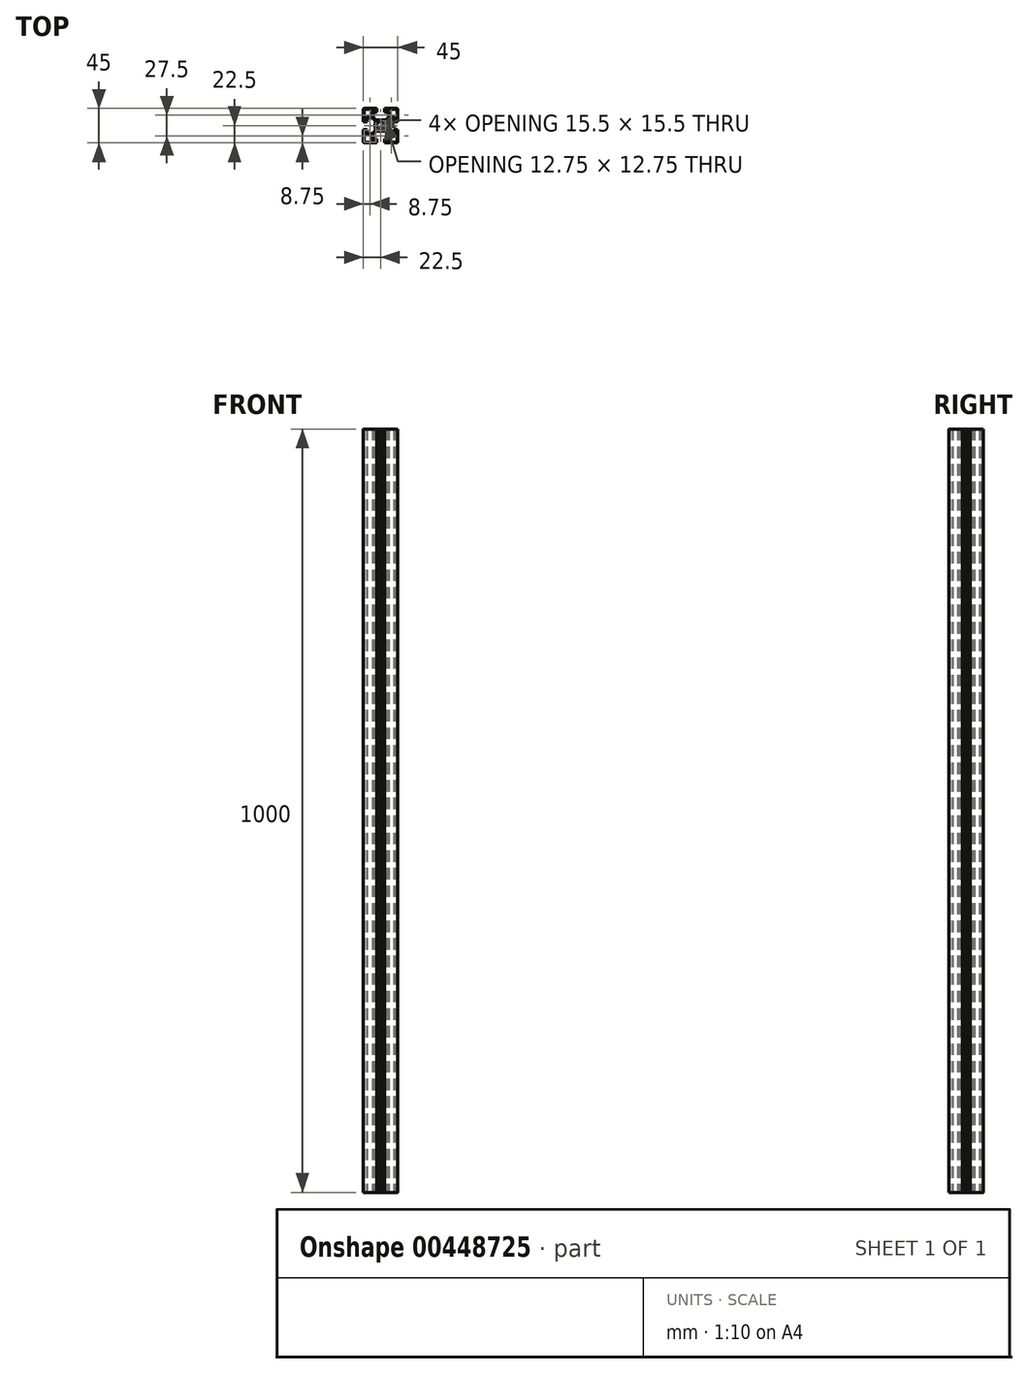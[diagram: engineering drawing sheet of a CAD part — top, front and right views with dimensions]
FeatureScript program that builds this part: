
annotation { "Feature Type Name" : "Feature", "Feature Type Description" : "" }
export const myFeature = defineFeature(function(context is Context, id is Id, definition is map)
    precondition{}
    {
        {
            var Q0;
            Q0=qCreatedBy(makeId("Top.planeOp"),FACE);
            var sketch = newSketch(context, id + "F0", { "sketchPlane" : qUnion([Q0])});
            skPoint(sketch, "E0.middle", {"position": v(0, 0) * mm});
            skLineSegment(sketch, "E1", {"start": v(0, -50.6) * mm, "end": v(0, -50.6) * mm});
            skPoint(sketch, "E1.endSnap0", {"position": v(0, -22.4) * mm});
            skLineSegment(sketch, "E2", {"start": v(-31.12, 0) * mm, "end": v(33.93, 0) * mm, "construction": true});
            skLineSegment(sketch, "E3.0", {"start": v(-5, 22.5) * mm, "end": v(-5, 17.5) * mm});
            skLineSegment(sketch, "E4.0", {"start": v(-22.5, 5) * mm, "end": v(-17.5, 5) * mm});
            skLineSegment(sketch, "E5.trimOffspring", {"start": v(-5, 22.5) * mm, "end": v(-21.5, 22.5) * mm});
            skLineSegment(sketch, "E6.trimOffspring", {"start": v(-22.5, 5) * mm, "end": v(-22.5, 21.5) * mm});
            skLineSegment(sketch, "E7.0", {"start": v(-10.7, 10) * mm, "end": v(-7.25, 6.54) * mm});
            skLineSegment(sketch, "E8.0", {"start": v(-21.5, 6.5) * mm, "end": v(-21.5, 21) * mm});
            skLineSegment(sketch, "E9.0", {"start": v(-6.5, 21.5) * mm, "end": v(-21, 21.5) * mm});
            skLineSegment(sketch, "E10.0", {"start": v(-6, 21) * mm, "end": v(-6, 19.04) * mm});
            skLineSegment(sketch, "E11.0", {"start": v(-22.5, 0) * mm, "end": v(22.5, 0) * mm});
            skLineSegment(sketch, "E12.0", {"start": v(-21, 6) * mm, "end": v(-19, 6) * mm});
            skLineSegment(sketch, "E13.trimOffspring", {"start": v(-9.63, 10.7) * mm, "end": v(-6.54, 7.25) * mm});
            skLineSegment(sketch, "E14.trimOffspring", {"start": v(-6.5, 18.54) * mm, "end": v(-10.5, 18.56) * mm});
            skLineSegment(sketch, "E15.trimOffspring", {"start": v(-5, 17.5) * mm, "end": v(-9.63, 17.5) * mm});
            skLineSegment(sketch, "E16.trimOffspring", {"start": v(-18.5, 6.5) * mm, "end": v(-18.5, 10.5) * mm});
            skLineSegment(sketch, "E17.trimOffspring", {"start": v(-17.5, 5) * mm, "end": v(-17.5, 10) * mm});
            skLineSegment(sketch, "E18.trimOffspring", {"start": v(-11, 11.5) * mm, "end": v(-11, 18.06) * mm});
            skLineSegment(sketch, "E19.trimOffspring", {"start": v(-11.5, 11) * mm, "end": v(-18, 11) * mm});
            skLineSegment(sketch, "E20.trimOffspring", {"start": v(-9.63, 10.7) * mm, "end": v(-9.63, 17.5) * mm});
            skLineSegment(sketch, "E21.trimOffspring", {"start": v(-10.7, 10) * mm, "end": v(-17.5, 10) * mm});
            skPoint(sketch, "E22.visualSharp", {"position": v(-22.5, 22.5) * mm});
            skArc(sketch, "E22.filletArc", {"start": v(-21.5, 22.5) * mm, "mid": v(-22.2, 22.2) * mm, "end": v(-22.5, 21.5) * mm});
            skArc(sketch, "E23.filletArc", {"start": v(-21, 21.5) * mm, "mid": v(-21.35, 21.35) * mm, "end": v(-21.5, 21) * mm});
            skPoint(sketch, "E24.visualSharp", {"position": v(-21.5, 6) * mm});
            skArc(sketch, "E24.filletArc", {"start": v(-21.5, 6.5) * mm, "mid": v(-21.35, 6.15) * mm, "end": v(-21, 6) * mm});
            skPoint(sketch, "E25.visualSharp", {"position": v(-18.5, 6) * mm});
            skArc(sketch, "E25.filletArc", {"start": v(-19, 6) * mm, "mid": v(-18.65, 6.15) * mm, "end": v(-18.5, 6.5) * mm});
            skPoint(sketch, "E26.visualSharp", {"position": v(-18.5, 11) * mm});
            skArc(sketch, "E26.filletArc", {"start": v(-18, 11) * mm, "mid": v(-18.35, 10.85) * mm, "end": v(-18.5, 10.5) * mm});
            skPoint(sketch, "E27.visualSharp", {"position": v(-11, 11) * mm});
            skArc(sketch, "E27.filletArc", {"start": v(-11.5, 11) * mm, "mid": v(-11.15, 11.15) * mm, "end": v(-11, 11.5) * mm});
            skPoint(sketch, "E28.visualSharp", {"position": v(-11, 18.56) * mm});
            skArc(sketch, "E28.filletArc", {"start": v(-10.5, 18.56) * mm, "mid": v(-10.85, 18.41) * mm, "end": v(-11, 18.06) * mm});
            skPoint(sketch, "E29.visualSharp", {"position": v(-6, 18.53) * mm});
            skArc(sketch, "E29.filletArc", {"start": v(-6.5, 18.54) * mm, "mid": v(-6.15, 18.68) * mm, "end": v(-6, 19.04) * mm});
            skPoint(sketch, "E30.visualSharp", {"position": v(-6, 21.5) * mm});
            skArc(sketch, "E30.filletArc", {"start": v(-6, 21) * mm, "mid": v(-6.15, 21.35) * mm, "end": v(-6.5, 21.5) * mm});
            skPoint(sketch, "E31.1.0", {"position": v(-18.5, -11) * mm});
            skLineSegment(sketch, "E31.1.1", {"start": v(-5, -17.5) * mm, "end": v(-10, -17.5) * mm});
            skLineSegment(sketch, "E31.1.2", {"start": v(-21.5, -6.5) * mm, "end": v(-21.5, -21) * mm});
            skLineSegment(sketch, "E31.1.3", {"start": v(-6.5, -21.5) * mm, "end": v(-21, -21.5) * mm});
            skLineSegment(sketch, "E31.1.4", {"start": v(-10, -10.7) * mm, "end": v(-6.54, -7.25) * mm});
            skLineSegment(sketch, "E31.1.5", {"start": v(-5, -22.5) * mm, "end": v(-21.5, -22.5) * mm});
            skLineSegment(sketch, "E31.1.6", {"start": v(-22.5, -5) * mm, "end": v(-22.5, -21.5) * mm});
            skPoint(sketch, "E31.1.7", {"position": v(-11, -11) * mm});
            skLineSegment(sketch, "E31.1.8", {"start": v(-6.5, -18.5) * mm, "end": v(-10.5, -18.5) * mm});
            skLineSegment(sketch, "E31.1.9", {"start": v(-17.5, -5) * mm, "end": v(-17.5, -10) * mm});
            skLineSegment(sketch, "E31.1.10", {"start": v(-18.5, -6.5) * mm, "end": v(-18.5, -10.5) * mm});
            skPoint(sketch, "E31.1.11", {"position": v(-18.5, -6) * mm});
            skPoint(sketch, "E31.1.12", {"position": v(-21.5, -21.5) * mm});
            skPoint(sketch, "E31.1.13", {"position": v(-11, -18.5) * mm});
            skLineSegment(sketch, "E31.1.14", {"start": v(-10, -10.7) * mm, "end": v(-10, -17.5) * mm});
            skLineSegment(sketch, "E31.1.15", {"start": v(-10.7, -10) * mm, "end": v(-7.25, -6.54) * mm});
            skLineSegment(sketch, "E31.1.16", {"start": v(-5, -22.5) * mm, "end": v(-5, -17.5) * mm});
            skLineSegment(sketch, "E31.1.17", {"start": v(-10.7, -10) * mm, "end": v(-17.5, -10) * mm});
            skPoint(sketch, "E31.1.18", {"position": v(-21.5, -6) * mm});
            skPoint(sketch, "E31.1.19", {"position": v(-6, -18.5) * mm});
            skLineSegment(sketch, "E31.1.20", {"start": v(-11, -11.5) * mm, "end": v(-11, -18) * mm});
            skLineSegment(sketch, "E31.1.21", {"start": v(-11.5, -11) * mm, "end": v(-18, -11) * mm});
            skPoint(sketch, "E31.1.22", {"position": v(-6, -21.5) * mm});
            skPoint(sketch, "E31.1.23", {"position": v(0.07, -0.4) * mm});
            skLineSegment(sketch, "E31.1.24", {"start": v(-22.5, -5) * mm, "end": v(-17.5, -5) * mm});
            skPoint(sketch, "E31.1.25", {"position": v(-22.5, -22.5) * mm});
            skArc(sketch, "E31.1.26", {"start": v(-22.5, -21.5) * mm, "mid": v(-22.2, -22.2) * mm, "end": v(-21.5, -22.5) * mm});
            skPoint(sketch, "E31.1.27", {"position": v(0.07, -0.4) * mm});
            skLineSegment(sketch, "E31.1.28", {"start": v(-6, -21) * mm, "end": v(-6, -19) * mm});
            skLineSegment(sketch, "E31.1.29", {"start": v(-21, -6) * mm, "end": v(-19, -6) * mm});
            skPoint(sketch, "E31.1.30", {"position": v(0.07, -0.4) * mm});
            skArc(sketch, "E31.1.31", {"start": v(-21.5, -21) * mm, "mid": v(-21.35, -21.35) * mm, "end": v(-21, -21.5) * mm});
            skPoint(sketch, "E31.1.32", {"position": v(0.07, -0.4) * mm});
            skArc(sketch, "E31.1.33", {"start": v(-6.5, -21.5) * mm, "mid": v(-6.15, -21.35) * mm, "end": v(-6, -21) * mm});
            skArc(sketch, "E31.1.34", {"start": v(-18.5, -6.5) * mm, "mid": v(-18.65, -6.15) * mm, "end": v(-19, -6) * mm});
            skArc(sketch, "E31.1.35", {"start": v(-11, -18) * mm, "mid": v(-10.85, -18.35) * mm, "end": v(-10.5, -18.5) * mm});
            skArc(sketch, "E31.1.36", {"start": v(-21, -6) * mm, "mid": v(-21.35, -6.15) * mm, "end": v(-21.5, -6.5) * mm});
            skArc(sketch, "E31.1.37", {"start": v(-11, -11.5) * mm, "mid": v(-11.15, -11.15) * mm, "end": v(-11.5, -11) * mm});
            skArc(sketch, "E31.1.38", {"start": v(-6, -19) * mm, "mid": v(-6.15, -18.65) * mm, "end": v(-6.5, -18.5) * mm});
            skArc(sketch, "E31.1.39", {"start": v(-18.5, -10.5) * mm, "mid": v(-18.35, -10.85) * mm, "end": v(-18, -11) * mm});
            skPoint(sketch, "E31.2.0", {"position": v(11, -18.5) * mm});
            skLineSegment(sketch, "E31.2.1", {"start": v(17.5, -5) * mm, "end": v(17.5, -10) * mm});
            skLineSegment(sketch, "E31.2.2", {"start": v(6.5, -21.5) * mm, "end": v(21, -21.5) * mm});
            skLineSegment(sketch, "E31.2.3", {"start": v(21.5, -6.5) * mm, "end": v(21.5, -21) * mm});
            skLineSegment(sketch, "E31.2.4", {"start": v(10.7, -10) * mm, "end": v(7.25, -6.54) * mm});
            skLineSegment(sketch, "E31.2.5", {"start": v(22.5, -5) * mm, "end": v(22.5, -21.5) * mm});
            skLineSegment(sketch, "E31.2.6", {"start": v(5, -22.5) * mm, "end": v(21.5, -22.5) * mm});
            skPoint(sketch, "E31.2.7", {"position": v(11, -11) * mm});
            skLineSegment(sketch, "E31.2.8", {"start": v(18.5, -6.5) * mm, "end": v(18.5, -10.5) * mm});
            skLineSegment(sketch, "E31.2.9", {"start": v(5, -17.5) * mm, "end": v(10, -17.5) * mm});
            skLineSegment(sketch, "E31.2.10", {"start": v(6.5, -18.5) * mm, "end": v(10.5, -18.5) * mm});
            skPoint(sketch, "E31.2.11", {"position": v(6, -18.5) * mm});
            skPoint(sketch, "E31.2.12", {"position": v(21.5, -21.5) * mm});
            skPoint(sketch, "E31.2.13", {"position": v(18.5, -11) * mm});
            skLineSegment(sketch, "E31.2.14", {"start": v(10.7, -10) * mm, "end": v(17.5, -10) * mm});
            skLineSegment(sketch, "E31.2.15", {"start": v(10, -10.7) * mm, "end": v(6.54, -7.25) * mm});
            skLineSegment(sketch, "E31.2.16", {"start": v(22.5, -5) * mm, "end": v(17.5, -5) * mm});
            skLineSegment(sketch, "E31.2.17", {"start": v(10, -10.7) * mm, "end": v(10, -17.5) * mm});
            skPoint(sketch, "E31.2.18", {"position": v(6, -21.5) * mm});
            skPoint(sketch, "E31.2.19", {"position": v(18.5, -6) * mm});
            skLineSegment(sketch, "E31.2.20", {"start": v(11.5, -11) * mm, "end": v(18, -11) * mm});
            skLineSegment(sketch, "E31.2.21", {"start": v(11, -11.5) * mm, "end": v(11, -18) * mm});
            skPoint(sketch, "E31.2.22", {"position": v(21.5, -6) * mm});
            skLineSegment(sketch, "E31.2.24", {"start": v(5, -22.5) * mm, "end": v(5, -17.5) * mm});
            skPoint(sketch, "E31.2.25", {"position": v(22.5, -22.5) * mm});
            skArc(sketch, "E31.2.26", {"start": v(21.5, -22.5) * mm, "mid": v(22.2, -22.2) * mm, "end": v(22.5, -21.5) * mm});
            skLineSegment(sketch, "E31.2.28", {"start": v(21, -6) * mm, "end": v(19, -6) * mm});
            skLineSegment(sketch, "E31.2.29", {"start": v(6, -21) * mm, "end": v(6, -19) * mm});
            skArc(sketch, "E31.2.31", {"start": v(21, -21.5) * mm, "mid": v(21.35, -21.35) * mm, "end": v(21.5, -21) * mm});
            skArc(sketch, "E31.2.33", {"start": v(21.5, -6.5) * mm, "mid": v(21.35, -6.15) * mm, "end": v(21, -6) * mm});
            skArc(sketch, "E31.2.34", {"start": v(6.5, -18.5) * mm, "mid": v(6.15, -18.65) * mm, "end": v(6, -19) * mm});
            skArc(sketch, "E31.2.35", {"start": v(18, -11) * mm, "mid": v(18.35, -10.85) * mm, "end": v(18.5, -10.5) * mm});
            skArc(sketch, "E31.2.36", {"start": v(6, -21) * mm, "mid": v(6.15, -21.35) * mm, "end": v(6.5, -21.5) * mm});
            skArc(sketch, "E31.2.37", {"start": v(11.5, -11) * mm, "mid": v(11.15, -11.15) * mm, "end": v(11, -11.5) * mm});
            skArc(sketch, "E31.2.38", {"start": v(19, -6) * mm, "mid": v(18.65, -6.15) * mm, "end": v(18.5, -6.5) * mm});
            skArc(sketch, "E31.2.39", {"start": v(10.5, -18.5) * mm, "mid": v(10.85, -18.35) * mm, "end": v(11, -18) * mm});
            skPoint(sketch, "E31.3.0", {"position": v(18.5, 11) * mm});
            skLineSegment(sketch, "E31.3.1", {"start": v(5, 17.5) * mm, "end": v(10, 17.5) * mm});
            skLineSegment(sketch, "E31.3.2", {"start": v(21.5, 6.5) * mm, "end": v(21.5, 21) * mm});
            skLineSegment(sketch, "E31.3.3", {"start": v(6.5, 21.5) * mm, "end": v(21, 21.5) * mm});
            skLineSegment(sketch, "E31.3.4", {"start": v(10, 10.7) * mm, "end": v(6.54, 7.25) * mm});
            skLineSegment(sketch, "E31.3.5", {"start": v(5, 22.5) * mm, "end": v(21.5, 22.5) * mm});
            skLineSegment(sketch, "E31.3.6", {"start": v(22.5, 5) * mm, "end": v(22.5, 21.5) * mm});
            skPoint(sketch, "E31.3.7", {"position": v(11, 11) * mm});
            skLineSegment(sketch, "E31.3.8", {"start": v(6.5, 18.5) * mm, "end": v(10.5, 18.5) * mm});
            skLineSegment(sketch, "E31.3.9", {"start": v(17.5, 5) * mm, "end": v(17.5, 10) * mm});
            skLineSegment(sketch, "E31.3.10", {"start": v(18.5, 6.5) * mm, "end": v(18.5, 10.5) * mm});
            skPoint(sketch, "E31.3.11", {"position": v(18.5, 6) * mm});
            skPoint(sketch, "E31.3.12", {"position": v(21.5, 21.5) * mm});
            skPoint(sketch, "E31.3.13", {"position": v(11, 18.5) * mm});
            skLineSegment(sketch, "E31.3.14", {"start": v(10, 10.7) * mm, "end": v(10, 17.5) * mm});
            skLineSegment(sketch, "E31.3.15", {"start": v(10.7, 10) * mm, "end": v(7.25, 6.54) * mm});
            skLineSegment(sketch, "E31.3.16", {"start": v(5, 22.5) * mm, "end": v(5, 17.5) * mm});
            skLineSegment(sketch, "E31.3.17", {"start": v(10.7, 10) * mm, "end": v(17.5, 10) * mm});
            skPoint(sketch, "E31.3.18", {"position": v(21.5, 6) * mm});
            skPoint(sketch, "E31.3.19", {"position": v(6, 18.5) * mm});
            skLineSegment(sketch, "E31.3.20", {"start": v(11, 11.5) * mm, "end": v(11, 18) * mm});
            skLineSegment(sketch, "E31.3.21", {"start": v(11.5, 11) * mm, "end": v(18, 11) * mm});
            skPoint(sketch, "E31.3.22", {"position": v(6, 21.5) * mm});
            skLineSegment(sketch, "E31.3.24", {"start": v(22.5, 5) * mm, "end": v(17.5, 5) * mm});
            skPoint(sketch, "E31.3.25", {"position": v(22.5, 22.5) * mm});
            skArc(sketch, "E31.3.26", {"start": v(22.5, 21.5) * mm, "mid": v(22.2, 22.2) * mm, "end": v(21.5, 22.5) * mm});
            skLineSegment(sketch, "E31.3.28", {"start": v(6, 21) * mm, "end": v(6, 19) * mm});
            skLineSegment(sketch, "E31.3.29", {"start": v(21, 6) * mm, "end": v(19, 6) * mm});
            skArc(sketch, "E31.3.31", {"start": v(21.5, 21) * mm, "mid": v(21.35, 21.35) * mm, "end": v(21, 21.5) * mm});
            skArc(sketch, "E31.3.33", {"start": v(6.5, 21.5) * mm, "mid": v(6.15, 21.35) * mm, "end": v(6, 21) * mm});
            skArc(sketch, "E31.3.34", {"start": v(18.5, 6.5) * mm, "mid": v(18.65, 6.15) * mm, "end": v(19, 6) * mm});
            skArc(sketch, "E31.3.35", {"start": v(11, 18) * mm, "mid": v(10.85, 18.35) * mm, "end": v(10.5, 18.5) * mm});
            skArc(sketch, "E31.3.36", {"start": v(21, 6) * mm, "mid": v(21.35, 6.15) * mm, "end": v(21.5, 6.5) * mm});
            skArc(sketch, "E31.3.37", {"start": v(11, 11.5) * mm, "mid": v(11.15, 11.15) * mm, "end": v(11.5, 11) * mm});
            skArc(sketch, "E31.3.38", {"start": v(6, 19) * mm, "mid": v(6.15, 18.65) * mm, "end": v(6.5, 18.5) * mm});
            skArc(sketch, "E31.3.39", {"start": v(18.5, 10.5) * mm, "mid": v(18.35, 10.85) * mm, "end": v(18, 11) * mm});
            skArc(sketch, "E32", {"start": v(-2.78, 4.16) * mm, "mid": v(-3.54, 3.54) * mm, "end": v(-4.16, 2.78) * mm});
            skArc(sketch, "E33", {"start": v(-1.27, 6.38) * mm, "mid": v(-2.49, 6) * mm, "end": v(-3.61, 5.4) * mm});
            skLineSegment(sketch, "E34.bottom", {"start": v(6.54, -7.25) * mm, "end": v(1.92, -7.25) * mm});
            skLineSegment(sketch, "E34.top", {"start": v(6.54, 7.25) * mm, "end": v(1.92, 7.25) * mm});
            skLineSegment(sketch, "E34.left", {"start": v(7.25, -6.54) * mm, "end": v(7.25, -1.92) * mm});
            skLineSegment(sketch, "E34.right", {"start": v(-7.25, -6.54) * mm, "end": v(-7.25, -1.92) * mm});
            skArc(sketch, "E35", {"start": v(-7.25, 1.92) * mm, "mid": v(-7.5, 0) * mm, "end": v(-7.25, -1.92) * mm});
            skLineSegment(sketch, "E36.trimOffspring", {"start": v(-1.92, 7.25) * mm, "end": v(-6.54, 7.25) * mm});
            skPoint(sketch, "E37.orphan", {"position": v(-7.25, 7.25) * mm});
            skLineSegment(sketch, "E38.trimOffspring", {"start": v(-7.25, 1.92) * mm, "end": v(-7.25, 6.54) * mm});
            skArc(sketch, "E39.trimOffspring", {"start": v(-1.92, -7.25) * mm, "mid": v(0, -7.5) * mm, "end": v(1.92, -7.25) * mm});
            skLineSegment(sketch, "E40.trimOffspring", {"start": v(-1.92, -7.25) * mm, "end": v(-6.54, -7.25) * mm});
            skArc(sketch, "E41.trimOffspring", {"start": v(7.25, -1.92) * mm, "mid": v(7.5, 0) * mm, "end": v(7.25, 1.92) * mm});
            skPoint(sketch, "E42.orphan", {"position": v(-7.25, -7.25) * mm});
            skPoint(sketch, "E43.orphan", {"position": v(7.25, -7.25) * mm});
            skLineSegment(sketch, "E44.trimOffspring", {"start": v(7.25, 1.92) * mm, "end": v(7.25, 6.54) * mm});
            skArc(sketch, "E45.trimOffspring", {"start": v(1.92, 7.25) * mm, "mid": v(0, 7.5) * mm, "end": v(-1.92, 7.25) * mm});
            skPoint(sketch, "E46.orphan", {"position": v(7.25, 7.25) * mm});
            skLineSegment(sketch, "E47", {"start": v(-0.98, 4.9) * mm, "end": v(-1.27, 6.38) * mm});
            skLineSegment(sketch, "E48", {"start": v(0.98, 4.9) * mm, "end": v(1.27, 6.38) * mm});
            skLineSegment(sketch, "E49", {"start": v(2.78, 4.16) * mm, "end": v(3.61, 5.4) * mm});
            skLineSegment(sketch, "E50", {"start": v(4.16, 2.78) * mm, "end": v(5.4, 3.61) * mm});
            skLineSegment(sketch, "E51", {"start": v(4.9, 0.98) * mm, "end": v(6.38, 1.27) * mm});
            skLineSegment(sketch, "E52", {"start": v(4.9, -0.98) * mm, "end": v(6.38, -1.27) * mm});
            skLineSegment(sketch, "E53", {"start": v(4.16, -2.78) * mm, "end": v(5.4, -3.61) * mm});
            skLineSegment(sketch, "E54", {"start": v(2.78, -4.16) * mm, "end": v(3.61, -5.4) * mm});
            skLineSegment(sketch, "E55", {"start": v(0.98, -4.9) * mm, "end": v(1.27, -6.38) * mm});
            skLineSegment(sketch, "E56", {"start": v(-0.98, -4.9) * mm, "end": v(-1.27, -6.38) * mm});
            skLineSegment(sketch, "E57", {"start": v(-2.78, -4.16) * mm, "end": v(-3.61, -5.4) * mm});
            skLineSegment(sketch, "E58", {"start": v(-4.16, -2.78) * mm, "end": v(-5.4, -3.61) * mm});
            skLineSegment(sketch, "E59", {"start": v(-4.8, -1.37) * mm, "end": v(-6.28, -1.66) * mm});
            skPoint(sketch, "E60.endSnap0", {"position": v(-7.25, 4.23) * mm});
            skLineSegment(sketch, "E61", {"start": v(-2.78, 4.16) * mm, "end": v(-3.61, 5.4) * mm});
            skLineSegment(sketch, "E62", {"start": v(-4.16, 2.78) * mm, "end": v(-5.4, 3.61) * mm});
            skLineSegment(sketch, "E63", {"start": v(-4.9, 0.98) * mm, "end": v(-6.38, 1.27) * mm});
            skLineSegment(sketch, "E64.trimOffspring", {"start": v(1.46, 7.36) * mm, "end": v(2.6, 13.04) * mm});
            skPoint(sketch, "E65.orphan", {"position": v(6.54, -4.37) * mm});
            skArc(sketch, "E66.trimOffspring", {"start": v(-5.4, 3.61) * mm, "mid": v(-6, 2.49) * mm, "end": v(-6.38, 1.27) * mm});
            skArc(sketch, "E67.trimOffspring", {"start": v(-4.9, 0.98) * mm, "mid": v(-5, -0.2) * mm, "end": v(-4.8, -1.37) * mm});
            skArc(sketch, "E68.trimOffspring", {"start": v(-6.28, -1.66) * mm, "mid": v(-5.92, -2.67) * mm, "end": v(-5.4, -3.61) * mm});
            skArc(sketch, "E69.trimOffspring", {"start": v(-4.16, -2.78) * mm, "mid": v(-3.54, -3.54) * mm, "end": v(-2.78, -4.16) * mm});
            skArc(sketch, "E70.trimOffspring", {"start": v(-3.61, -5.4) * mm, "mid": v(-2.49, -6) * mm, "end": v(-1.27, -6.38) * mm});
            skArc(sketch, "E71.trimOffspring", {"start": v(-0.98, -4.9) * mm, "mid": v(0, -5) * mm, "end": v(0.98, -4.9) * mm});
            skArc(sketch, "E72.trimOffspring", {"start": v(1.27, -6.38) * mm, "mid": v(2.49, -6) * mm, "end": v(3.61, -5.4) * mm});
            skArc(sketch, "E73.trimOffspring", {"start": v(2.78, -4.16) * mm, "mid": v(3.54, -3.54) * mm, "end": v(4.16, -2.78) * mm});
            skArc(sketch, "E74.trimOffspring", {"start": v(5.4, -3.61) * mm, "mid": v(6, -2.49) * mm, "end": v(6.38, -1.27) * mm});
            skArc(sketch, "E75.trimOffspring", {"start": v(4.9, -0.98) * mm, "mid": v(5, 0) * mm, "end": v(4.9, 0.98) * mm});
            skArc(sketch, "E76.trimOffspring", {"start": v(6.38, 1.27) * mm, "mid": v(6, 2.49) * mm, "end": v(5.4, 3.61) * mm});
            skArc(sketch, "E77.trimOffspring", {"start": v(4.16, 2.78) * mm, "mid": v(3.54, 3.54) * mm, "end": v(2.78, 4.16) * mm});
            skArc(sketch, "E78.trimOffspring", {"start": v(3.61, 5.4) * mm, "mid": v(2.49, 6) * mm, "end": v(1.27, 6.38) * mm});
            skArc(sketch, "E79.trimOffspring", {"start": v(0.98, 4.9) * mm, "mid": v(0, 5) * mm, "end": v(-0.98, 4.9) * mm});
            skSolve(sketch);
        }
        {
            var Q0;
            Q0=qSketchRegion(id+"F0",true);
            extrude(context, id + "F1", {"entities" : qUnion([Q0]), "endBound" : BoundingType.SYMMETRIC, "depth" : 1000 * mm});
        }
    });
